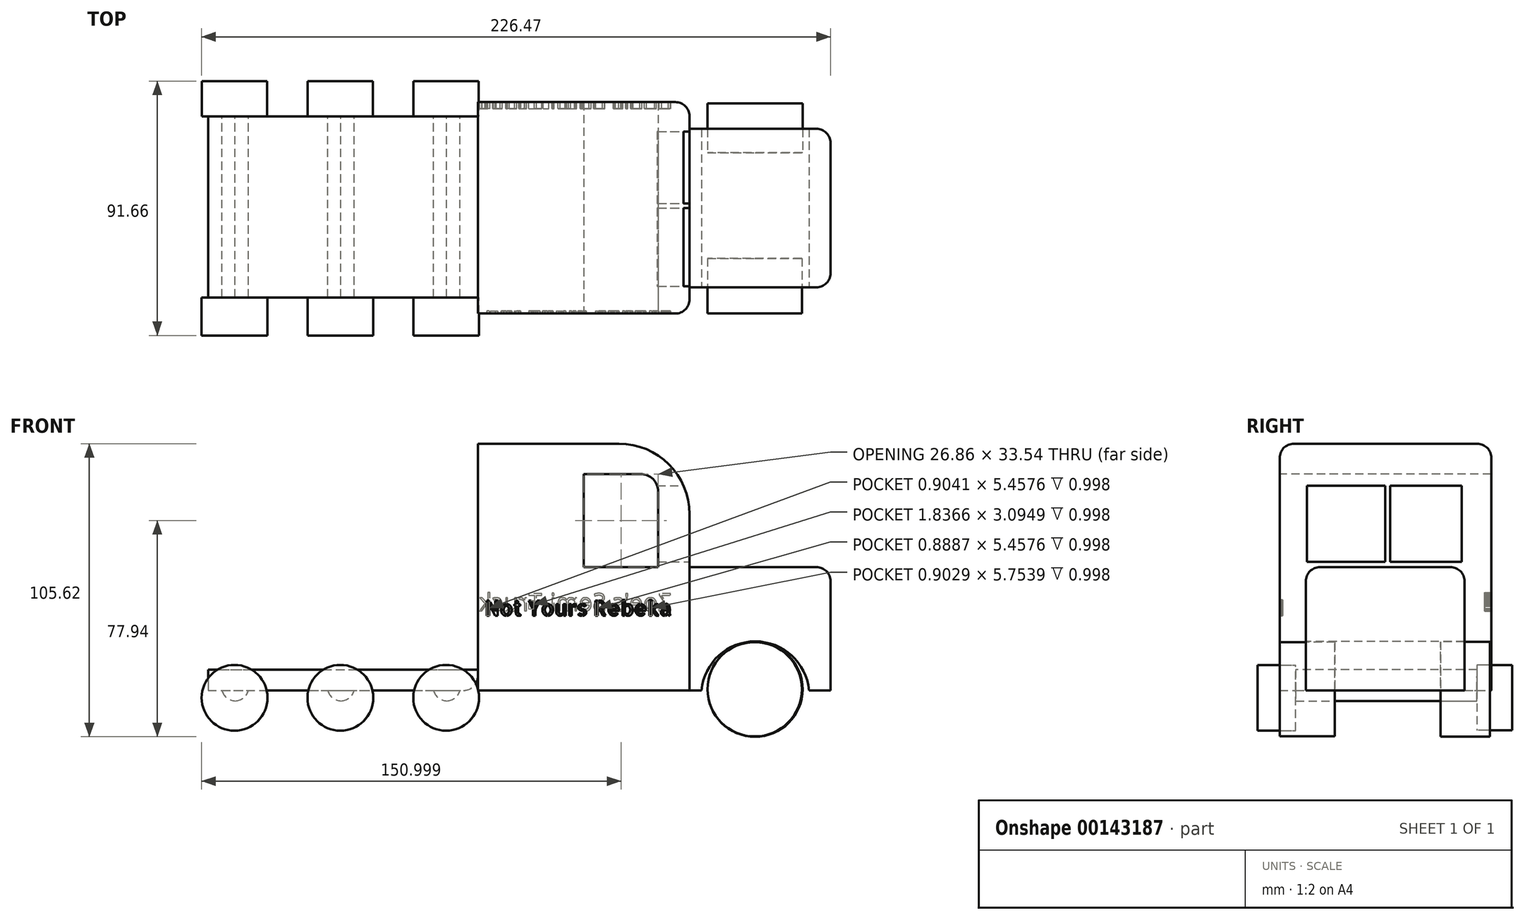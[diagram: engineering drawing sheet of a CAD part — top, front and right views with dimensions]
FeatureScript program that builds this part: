
annotation { "Feature Type Name" : "Feature", "Feature Type Description" : "" }
export const myFeature = defineFeature(function(context is Context, id is Id, definition is map)
    precondition{}
    {
        {
            var Q0;
            Q0=qCreatedBy(makeId("Front.planeOp"),FACE);
            var sketch = newSketch(context, id + "F0", { "sketchPlane" : qUnion([Q0])});
            skLineSegment(sketch, "E0.bottom", {"start": v(-38.1, 44.45) * mm, "end": v(38.1, 44.45) * mm});
            skLineSegment(sketch, "E0.top", {"start": v(-38.1, -44.45) * mm, "end": v(38.1, -44.45) * mm});
            skLineSegment(sketch, "E0.left", {"start": v(-38.1, 44.45) * mm, "end": v(-38.1, -44.45) * mm});
            skLineSegment(sketch, "E0.right", {"start": v(38.1, 44.45) * mm, "end": v(38.1, -44.45) * mm});
            skPoint(sketch, "E0.middle", {"position": v(0, 0) * mm});
            skSolve(sketch);
        }
        {
            var Q0;
            Q0 = qSketchRegion(id + "F0", true);
            extrude(context, id + "F1", {"entities" : qUnion([Q0]), "depth" : 76.2 * mm});
        }
        {
            var Q0;
            Q0=makeQuery(id+"F1.opExtrude","SWEPT_EDGE",EDGE,{"disambiguationData":[OSD([sQuery(id+"F0.wireOp",EDGE,"E0.bottom"),sQuery(id+"F0.wireOp",EDGE,"E0.right")])]});
            fillet(context, id + "F2", {"entities" : qUnion([Q0]), "radius" : 25.4 * mm, "tangentPropagation" : true, "allowEdgeOverflow" : false});
        }
        {
            var Q0;
            {var subQ0=sQuery(id+"F0.wireOp",EDGE,"E0.right");var subQ1=sQuery(id+"F0.wireOp",EDGE,"E0.bottom");Q0=makeQuery(id+"F2.opFillet","BLEND_EDGE",EDGE,{"blendedFrom":[makeQuery(id+"F1.opExtrude","SWEPT_EDGE",EDGE,{"disambiguationData":[OSD([subQ1,subQ0])]}),makeQuery(id+"F1.opExtrude","CAP_FACE",FACE,{"disambiguationData":[OSD([subQ1,sQuery(id+"F0.wireOp",EDGE,"E0.top"),sQuery(id+"F0.wireOp",EDGE,"E0.left"),subQ0])],"isStart":true})],"blendedInto":[makeQuery(id+"F1.opExtrude","CAP_FACE",FACE,{"disambiguationData":[OSD([subQ1,sQuery(id+"F0.wireOp",EDGE,"E0.top"),sQuery(id+"F0.wireOp",EDGE,"E0.left"),subQ0])],"isStart":true})]});}
            fillet(context, id + "F3", {"entities" : qUnion([Q0]), "radius" : 5.08 * mm, "tangentPropagation" : true, "allowEdgeOverflow" : false});
        }
        {
            var Q0;
            Q0=makeQuery(id+"F1.opExtrude","CAP_EDGE",EDGE,{"disambiguationData":[OSD([sQuery(id+"F0.wireOp",EDGE,"E0.bottom")])],"isStart":false});
            fillet(context, id + "F4", {"entities" : qUnion([Q0]), "radius" : 5.08 * mm, "tangentPropagation" : true, "allowEdgeOverflow" : false});
        }
        {
            var Q0;
            Q0=makeQuery(id+"F1.opExtrude","SWEPT_FACE",FACE,{"disambiguationData":[OSD([sQuery(id+"F0.wireOp",EDGE,"E0.right")])]});
            var sketch = newSketch(context, id + "F5", { "sketchPlane" : qUnion([Q0])});
            skLineSegment(sketch, "E1.bottom", {"start": v(-66.78, 0) * mm, "end": v(-9.63, 0) * mm});
            skLineSegment(sketch, "E1.top", {"start": v(-66.78, -44.45) * mm, "end": v(-9.63, -44.45) * mm});
            skLineSegment(sketch, "E1.left", {"start": v(-66.78, 0) * mm, "end": v(-66.78, -44.45) * mm});
            skLineSegment(sketch, "E1.right", {"start": v(-9.63, 0) * mm, "end": v(-9.63, -44.45) * mm});
            skSolve(sketch);
        }
        {
            var Q0;
            Q0=makeQuery(id+"F5.imprint","IMPRINT",FACE,{"disambiguationData":[TD([[makeQuery(id+"F5.imprint","IMPRINT",EDGE,{"derivedFrom":sQuery(id+"F5.wireOp",EDGE,"E1.bottom")}),-1.0]])]});
            extrude(context, id + "F6", {"entities" : qUnion([Q0]), "operationType" : NewBodyOperationType.ADD, "depth" : 50.8 * mm});
        }
        {
            var Q0;
            Q0=makeQuery(id+"F6.opExtrude","CAP_EDGE",EDGE,{"disambiguationData":[OSD([sQuery(id+"F5.wireOp",EDGE,"E1.bottom")])],"isStart":false});
            var Q1;
            Q1=makeQuery(id+"F6.opExtrude","SWEPT_EDGE",EDGE,{"disambiguationData":[OSD([sQuery(id+"F5.wireOp",EDGE,"E1.bottom"),sQuery(id+"F5.wireOp",EDGE,"E1.right")])]});
            var Q2;
            Q2=makeQuery(id+"F6.opExtrude","SWEPT_EDGE",EDGE,{"disambiguationData":[OSD([sQuery(id+"F5.wireOp",EDGE,"E1.bottom"),sQuery(id+"F5.wireOp",EDGE,"E1.left")])]});
            var Q3;
            Q3=makeQuery(id+"F6.opExtrude","CAP_EDGE",EDGE,{"disambiguationData":[OSD([sQuery(id+"F5.wireOp",EDGE,"E1.left")])],"isStart":false});
            var Q4;
            Q4=makeQuery(id+"F6.opExtrude","CAP_EDGE",EDGE,{"disambiguationData":[OSD([sQuery(id+"F5.wireOp",EDGE,"E1.right")])],"isStart":false});
            fillet(context, id + "F7", {"entities" : qUnion([Q0, Q1, Q2, Q3, Q4]), "radius" : 5.08 * mm, "tangentPropagation" : true, "allowEdgeOverflow" : false});
        }
        {
            var Q0;
            Q0=makeQuery(id+"F6.opExtrude","SWEPT_FACE",FACE,{"disambiguationData":[OSD([sQuery(id+"F5.wireOp",EDGE,"E1.left")])]});
            var sketch = newSketch(context, id + "F8", { "sketchPlane" : qUnion([Q0])});
            skCircle(sketch, "E2", {"center": v(61.81, -46.27) * mm, "radius": 19.46 * mm});
            skSolve(sketch);
        }
        {
            var Q0;
            {var subQ0=sQuery(id+"F8.wireOp",EDGE,"E2");var subQ1=makeQuery(id+"F6.opExtrude","SWEPT_EDGE",EDGE,{"disambiguationData":[OSD([sQuery(id+"F0.wireOp",EDGE,"E0.top"),sQuery(id+"F0.wireOp",EDGE,"E0.right"),sQuery(id+"F5.wireOp",EDGE,"E1.top"),sQuery(id+"F5.wireOp",EDGE,"E1.left")])]});var subQ2=makeQuery(id+"F8.imprint","INTERSECT",VERTEX,{"disambiguationData":[OD(0.0)],"derivedFrom":[subQ1,subQ0]});Q0=makeQuery(id+"F8.imprint","IMPRINT",FACE,{"disambiguationData":[TD([[makeQuery(id+"F8.imprint","IMPRINT",EDGE,{"disambiguationData":[TD([[subQ2,1.0]])],"derivedFrom":subQ0}),1.0]])]});}
            extrude(context, id + "F9", {"entities" : qUnion([Q0]), "operationType" : NewBodyOperationType.REMOVE, "oppositeDirection" : true, "depth" : 198.74 * mm});
        }
        {
            var Q0;
            Q0=makeQuery(id+"F1.opExtrude","CAP_FACE",FACE,{"disambiguationData":[OSD([sQuery(id+"F0.wireOp",EDGE,"E0.bottom"),sQuery(id+"F0.wireOp",EDGE,"E0.top"),sQuery(id+"F0.wireOp",EDGE,"E0.left"),sQuery(id+"F0.wireOp",EDGE,"E0.right")])],"isStart":false});
            var sketch = newSketch(context, id + "F10", { "sketchPlane" : qUnion([Q0])});
            skLineSegment(sketch, "E3.bottom", {"start": v(0, 33.54) * mm, "end": v(20.5, 33.54) * mm});
            skLineSegment(sketch, "E3.top", {"start": v(0, 0) * mm, "end": v(26.86, 0) * mm});
            skLineSegment(sketch, "E3.left", {"start": v(0, 33.54) * mm, "end": v(0, 0) * mm});
            skLineSegment(sketch, "E3.right", {"start": v(26.86, 27.19) * mm, "end": v(26.86, 0) * mm});
            skPoint(sketch, "E4.visualSharp", {"position": v(26.86, 33.54) * mm});
            skArc(sketch, "E4.filletArc", {"start": v(26.86, 27.19) * mm, "mid": v(25, 31.68) * mm, "end": v(20.5, 33.54) * mm});
            skSolve(sketch);
        }
        {
            var Q0;
            Q0=makeQuery(id+"F10.imprint","IMPRINT",FACE,{"disambiguationData":[TD([[makeQuery(id+"F10.imprint","IMPRINT",EDGE,{"derivedFrom":sQuery(id+"F10.wireOp",EDGE,"E3.bottom")}),-1.0]])]});
            extrude(context, id + "F11", {"entities" : qUnion([Q0]), "operationType" : NewBodyOperationType.REMOVE, "oppositeDirection" : true, "depth" : 169.3 * mm});
        }
        {
            var Q0;
            Q0=makeQuery(id+"F1.opExtrude","SWEPT_FACE",FACE,{"disambiguationData":[OSD([sQuery(id+"F0.wireOp",EDGE,"E0.right")])]});
            var sketch = newSketch(context, id + "F12", { "sketchPlane" : qUnion([Q0])});
            skPoint(sketch, "E5.oppositeSnap0", {"position": v(-38.2, 0) * mm});
            skLineSegment(sketch, "E5.bottom", {"start": v(-66.37, 29.3) * mm, "end": v(-38.2, 29.3) * mm});
            skLineSegment(sketch, "E5.top", {"start": v(-66.37, 1.82) * mm, "end": v(-38.2, 1.82) * mm});
            skLineSegment(sketch, "E5.left", {"start": v(-66.37, 29.3) * mm, "end": v(-66.37, 1.82) * mm});
            skLineSegment(sketch, "E5.right", {"start": v(-38.2, 29.3) * mm, "end": v(-38.2, 1.82) * mm});
            skLineSegment(sketch, "E6.bottom", {"start": v(-36.47, 29.3) * mm, "end": v(-10.6, 29.3) * mm});
            skLineSegment(sketch, "E6.top", {"start": v(-36.47, 1.82) * mm, "end": v(-10.6, 1.82) * mm});
            skLineSegment(sketch, "E6.left", {"start": v(-36.47, 29.3) * mm, "end": v(-36.47, 1.82) * mm});
            skLineSegment(sketch, "E6.right", {"start": v(-10.6, 29.3) * mm, "end": v(-10.6, 1.82) * mm});
            skSolve(sketch);
        }
        {
            var Q0;
            Q0 = qSketchRegion(id + "F12", true);
            extrude(context, id + "F13", {"entities" : qUnion([Q0]), "operationType" : NewBodyOperationType.REMOVE, "oppositeDirection" : true, "depth" : 25.4 * mm});
        }
        {
            var Q0;
            Q0=makeQuery(id+"F1.opExtrude","CAP_FACE",FACE,{"disambiguationData":[OSD([sQuery(id+"F0.wireOp",EDGE,"E0.bottom"),sQuery(id+"F0.wireOp",EDGE,"E0.top"),sQuery(id+"F0.wireOp",EDGE,"E0.left"),sQuery(id+"F0.wireOp",EDGE,"E0.right")])],"isStart":true});
            var sketch = newSketch(context, id + "F14", { "sketchPlane" : qUnion([Q0])});
            skText(sketch, "E7", { "text": "Zoe\'s Semi-Truck", "fontName": "OpenSans-Regular.ttf"});
            const initialGuessF14  = {"E7": [-0.03177, -0.01583, 1, 0, 0.00634]};
            skSetInitialGuess(sketch, initialGuessF14);
            skSolve(sketch);
        }
        {
            var Q0;
            Q0 = qSketchRegion(id + "F14", true);
            extrude(context, id + "F15", {"entities" : qUnion([Q0]), "operationType" : NewBodyOperationType.REMOVE, "oppositeDirection" : true, "depth" : 2.36 * mm});
        }
        {
            var Q0;
            Q0=makeQuery(id+"F1.opExtrude","CAP_FACE",FACE,{"disambiguationData":[OSD([sQuery(id+"F0.wireOp",EDGE,"E0.bottom"),sQuery(id+"F0.wireOp",EDGE,"E0.top"),sQuery(id+"F0.wireOp",EDGE,"E0.left"),sQuery(id+"F0.wireOp",EDGE,"E0.right")])],"isStart":false});
            var sketch = newSketch(context, id + "F16", { "sketchPlane" : qUnion([Q0])});
            skText(sketch, "E8", { "text": "Not Yours Rebeka", "fontName": "AllertaStencil-Regular.ttf"});
            skPoint(sketch, "E9", {"position": v(33.02, -12.7) * mm});
            const initialGuessF16  = {"E8": [-0.03557, -0.01755, 1, 0, 0.00546]};
            skSetInitialGuess(sketch, initialGuessF16);
            skSolve(sketch);
        }
        {
            var Q0;
            Q0 = qSketchRegion(id + "F16", true);
            extrude(context, id + "F17", {"entities" : qUnion([Q0]), "operationType" : NewBodyOperationType.REMOVE, "oppositeDirection" : true, "depth" : 1 * mm});
        }
        {
            var Q0;
            Q0=makeQuery(id+"F1.opExtrude","CAP_FACE",FACE,{"disambiguationData":[OSD([sQuery(id+"F0.wireOp",EDGE,"E0.bottom"),sQuery(id+"F0.wireOp",EDGE,"E0.top"),sQuery(id+"F0.wireOp",EDGE,"E0.left"),sQuery(id+"F0.wireOp",EDGE,"E0.right")])],"isStart":false});
            var sketch = newSketch(context, id + "F18", { "sketchPlane" : qUnion([Q0])});
            skCircle(sketch, "E10", {"center": v(61.6, -44.05) * mm, "radius": 16.98 * mm});
            skSolve(sketch);
        }
        {
            var Q0;
            Q0=makeQuery(id+"F18.imprint","IMPRINT",FACE,{"disambiguationData":[TD([[makeQuery(id+"F18.imprint","IMPRINT",EDGE,{"derivedFrom":sQuery(id+"F18.wireOp",EDGE,"E10")}),1.0]])]});
            extrude(context, id + "F19", {"entities" : qUnion([Q0]), "oppositeDirection" : true, "depth" : 19.87 * mm});
        }
        {
            var Q0;
            Q0=makeQuery(id+"F6.opExtrude","SWEPT_FACE",FACE,{"disambiguationData":[OSD([sQuery(id+"F5.wireOp",EDGE,"E1.right")])]});
            var sketch = newSketch(context, id + "F20", { "sketchPlane" : qUnion([Q0])});
            skCircle(sketch, "E11", {"center": v(-61.73, -44.04) * mm, "radius": 17.13 * mm});
            skPoint(sketch, "E11.first.point", {"position": v(-78.38, -40) * mm});
            skPoint(sketch, "E11.second.point", {"position": v(-45.04, -47.88) * mm});
            skPoint(sketch, "E11.third.point", {"position": v(-64.03, -61.02) * mm});
            skSolve(sketch);
        }
        {
            var Q0;
            Q0=makeQuery(id+"F20.imprint","IMPRINT",FACE,{"disambiguationData":[TD([[makeQuery(id+"F20.imprint","IMPRINT",EDGE,{"derivedFrom":sQuery(id+"F20.wireOp",EDGE,"E11")}),1.0]])]});
            extrude(context, id + "F21", {"entities" : qUnion([Q0]), "depth" : 9.14 * mm});
        }
        {
            var Q0;
            Q0 = qSketchRegion(id + "F20", true);
            extrude(context, id + "F22", {"entities" : qUnion([Q0]), "operationType" : NewBodyOperationType.ADD, "oppositeDirection" : true, "depth" : 8.57 * mm});
        }
        {
            var Q0;
            Q0=makeQuery(id+"F1.opExtrude","SWEPT_FACE",FACE,{"disambiguationData":[OSD([sQuery(id+"F0.wireOp",EDGE,"E0.left")])]});
            var sketch = newSketch(context, id + "F23", { "sketchPlane" : qUnion([Q0])});
            skLineSegment(sketch, "E12.bottom", {"start": v(5.15, -36.97) * mm, "end": v(70.41, -36.97) * mm});
            skLineSegment(sketch, "E12.top", {"start": v(5.15, -44.45) * mm, "end": v(70.41, -44.45) * mm});
            skLineSegment(sketch, "E12.left", {"start": v(5.15, -36.97) * mm, "end": v(5.15, -44.45) * mm});
            skLineSegment(sketch, "E12.right", {"start": v(70.41, -36.97) * mm, "end": v(70.41, -44.45) * mm});
            skSolve(sketch);
        }
        {
            var Q0;
            Q0 = qSketchRegion(id + "F23", true);
            extrude(context, id + "F24", {"entities" : qUnion([Q0]), "depth" : 97.15 * mm});
        }
        {
            var Q0;
            Q0=makeQuery(id+"F24.opExtrude","SWEPT_FACE",FACE,{"disambiguationData":[OSD([sQuery(id+"F23.wireOp",EDGE,"E12.left")])]});
            var sketch = newSketch(context, id + "F25", { "sketchPlane" : qUnion([Q0])});
            skCircle(sketch, "E13", {"center": v(49.54, -47.08) * mm, "radius": 11.75 * mm});
            skCircle(sketch, "E14.1.0.0", {"center": v(87.64, -47.08) * mm, "radius": 11.75 * mm});
            skCircle(sketch, "E14.2.0.0", {"center": v(125.74, -47.08) * mm, "radius": 11.75 * mm});
            skLineSegment(sketch, "E14.direction1", {"start": v(49.54, -47.08) * mm, "end": v(87.64, -47.08) * mm, "construction": true});
            skSolve(sketch);
        }
        {
            var Q0;
            Q0 = qSketchRegion(id + "F25", true);
            extrude(context, id + "F26", {"entities" : qUnion([Q0]), "depth" : 12.7 * mm});
        }
        {
            var Q0;
            Q0=makeQuery(id+"F24.opExtrude","SWEPT_FACE",FACE,{"disambiguationData":[OSD([sQuery(id+"F23.wireOp",EDGE,"E12.top")])]});
            var sketch = newSketch(context, id + "F27", { "sketchPlane" : qUnion([Q0])});
            skLineSegment(sketch, "E15.bottom", {"start": v(-130.27, 70.41) * mm, "end": v(-120.77, 70.41) * mm});
            skLineSegment(sketch, "E15.top", {"start": v(-130.27, 5.15) * mm, "end": v(-120.77, 5.15) * mm});
            skLineSegment(sketch, "E15.left", {"start": v(-130.27, 70.41) * mm, "end": v(-130.27, 5.15) * mm});
            skLineSegment(sketch, "E15.right", {"start": v(-120.77, 70.41) * mm, "end": v(-120.77, 5.15) * mm});
            skLineSegment(sketch, "E16.1.0.0", {"start": v(-92.17, 70.41) * mm, "end": v(-92.17, 5.15) * mm});
            skLineSegment(sketch, "E16.1.0.1", {"start": v(-82.67, 70.41) * mm, "end": v(-82.67, 5.15) * mm});
            skLineSegment(sketch, "E16.1.0.2", {"start": v(-92.17, 70.41) * mm, "end": v(-82.67, 70.41) * mm});
            skLineSegment(sketch, "E16.1.0.3", {"start": v(-92.17, 5.15) * mm, "end": v(-82.67, 5.15) * mm});
            skLineSegment(sketch, "E16.2.0.0", {"start": v(-54.07, 70.41) * mm, "end": v(-54.07, 5.15) * mm});
            skLineSegment(sketch, "E16.2.0.1", {"start": v(-44.57, 70.41) * mm, "end": v(-44.57, 5.15) * mm});
            skLineSegment(sketch, "E16.2.0.2", {"start": v(-54.07, 70.41) * mm, "end": v(-44.57, 70.41) * mm});
            skLineSegment(sketch, "E16.2.0.3", {"start": v(-54.07, 5.15) * mm, "end": v(-44.57, 5.15) * mm});
            skLineSegment(sketch, "E16.direction1", {"start": v(-130.27, 5.15) * mm, "end": v(-92.17, 5.15) * mm, "construction": true});
            skSolve(sketch);
        }
        {
            var Q0;
            Q0 = qSketchRegion(id + "F27", true);
            extrude(context, id + "F28", {"entities" : qUnion([Q0]), "depth" : 3.8 * mm});
        }
        {
            var Q0;
            Q0=makeQuery(id+"F28.opExtrude","CAP_EDGE",EDGE,{"disambiguationData":[OSD([sQuery(id+"F27.wireOp",EDGE,"E15.left")])],"isStart":false});
            var Q1;
            Q1=makeQuery(id+"F28.opExtrude","CAP_EDGE",EDGE,{"disambiguationData":[OSD([sQuery(id+"F27.wireOp",EDGE,"E15.right")])],"isStart":false});
            var Q2;
            Q2=makeQuery(id+"F28.opExtrude","CAP_EDGE",EDGE,{"disambiguationData":[OSD([sQuery(id+"F27.wireOp",EDGE,"E16.1.0.0")])],"isStart":false});
            var Q3;
            Q3=makeQuery(id+"F28.opExtrude","CAP_EDGE",EDGE,{"disambiguationData":[OSD([sQuery(id+"F27.wireOp",EDGE,"E16.1.0.1")])],"isStart":false});
            var Q4;
            Q4=makeQuery(id+"F28.opExtrude","CAP_EDGE",EDGE,{"disambiguationData":[OSD([sQuery(id+"F27.wireOp",EDGE,"E16.2.0.0")])],"isStart":false});
            var Q5;
            Q5=makeQuery(id+"F24.opExtrude","CAP_EDGE",EDGE,{"disambiguationData":[OSD([sQuery(id+"F23.wireOp",EDGE,"E12.top")])],"isStart":true});
            fillet(context, id + "F29", {"entities" : qUnion([Q0, Q1, Q2, Q3, Q4, Q5]), "radius" : 5.08 * mm, "tangentPropagation" : true, "allowEdgeOverflow" : false});
        }
        {
            var Q0;
            Q0=makeQuery(id+"F28.opExtrude","CAP_EDGE",EDGE,{"disambiguationData":[OSD([sQuery(id+"F27.wireOp",EDGE,"E16.2.0.1")])],"isStart":false});
            fillet(context, id + "F30", {"entities" : qUnion([Q0]), "radius" : 5.08 * mm, "tangentPropagation" : true, "allowEdgeOverflow" : false});
        }
        {
            var Q0;
            Q0=makeQuery(id+"F24.opExtrude","SWEPT_FACE",FACE,{"disambiguationData":[OSD([sQuery(id+"F23.wireOp",EDGE,"E12.right")])]});
            var sketch = newSketch(context, id + "F31", { "sketchPlane" : qUnion([Q0])});
            skCircle(sketch, "E17", {"center": v(-125.73, -47.13) * mm, "radius": 11.84 * mm});
            skPoint(sketch, "E17.first.point", {"position": v(-137.54, -46.27) * mm});
            skPoint(sketch, "E17.second.point", {"position": v(-113.9, -47.68) * mm});
            skPoint(sketch, "E17.third.point", {"position": v(-120.57, -57.79) * mm});
            skCircle(sketch, "E18.1.0.0", {"center": v(-87.63, -47.13) * mm, "radius": 11.84 * mm});
            skCircle(sketch, "E18.2.0.0", {"center": v(-49.53, -47.13) * mm, "radius": 11.84 * mm});
            skLineSegment(sketch, "E18.direction1", {"start": v(-125.73, -47.13) * mm, "end": v(-87.63, -47.13) * mm, "construction": true});
            skSolve(sketch);
        }
        {
            var Q0;
            Q0 = qSketchRegion(id + "F31", true);
            extrude(context, id + "F32", {"entities" : qUnion([Q0]), "depth" : 13.7 * mm});
        }
    });
